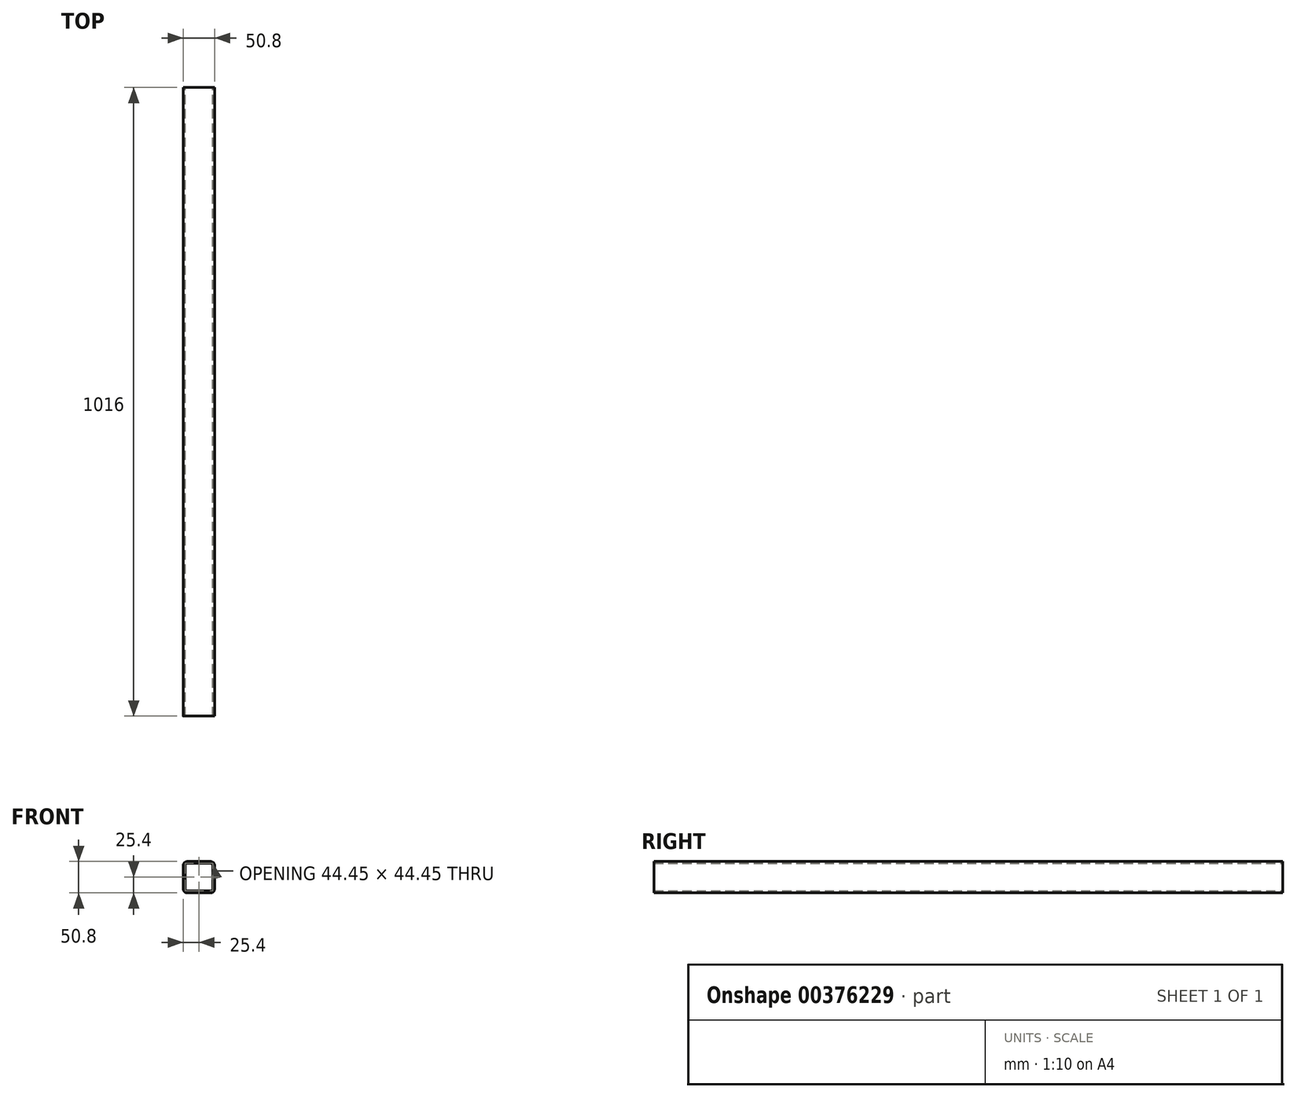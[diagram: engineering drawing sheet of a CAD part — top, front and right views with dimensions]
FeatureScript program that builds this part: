
annotation { "Feature Type Name" : "Feature", "Feature Type Description" : "" }
export const myFeature = defineFeature(function(context is Context, id is Id, definition is map)
    precondition{}
    {
        {
            var Q0;
            Q0=qCreatedBy(makeId("Front.planeOp"),FACE);
            var sketch = newSketch(context, id + "F0", { "sketchPlane" : qUnion([Q0])});
            skLineSegment(sketch, "E0.bottom", {"start": v(19.05, 25.4) * mm, "end": v(-19.05, 25.4) * mm});
            skLineSegment(sketch, "E0.top", {"start": v(19.05, -25.4) * mm, "end": v(-19.05, -25.4) * mm});
            skLineSegment(sketch, "E0.left", {"start": v(25.4, 19.05) * mm, "end": v(25.4, -19.05) * mm});
            skLineSegment(sketch, "E0.right", {"start": v(-25.4, 19.05) * mm, "end": v(-25.4, -19.05) * mm});
            skPoint(sketch, "E0.middle", {"position": v(0, 0) * mm});
            skPoint(sketch, "E1.visualSharp", {"position": v(-25.4, 25.4) * mm});
            skArc(sketch, "E1.filletArc", {"start": v(-19.05, 25.4) * mm, "mid": v(-23.54, 23.54) * mm, "end": v(-25.4, 19.05) * mm});
            skPoint(sketch, "E2.visualSharp", {"position": v(25.4, 25.4) * mm});
            skArc(sketch, "E2.filletArc", {"start": v(25.4, 19.05) * mm, "mid": v(23.54, 23.54) * mm, "end": v(19.05, 25.4) * mm});
            skPoint(sketch, "E3.visualSharp", {"position": v(25.4, -25.4) * mm});
            skArc(sketch, "E3.filletArc", {"start": v(19.05, -25.4) * mm, "mid": v(23.54, -23.54) * mm, "end": v(25.4, -19.05) * mm});
            skPoint(sketch, "E4.visualSharp", {"position": v(-25.4, -25.4) * mm});
            skArc(sketch, "E4.filletArc", {"start": v(-25.4, -19.05) * mm, "mid": v(-23.54, -23.54) * mm, "end": v(-19.05, -25.4) * mm});
            skArc(sketch, "E5.0", {"start": v(22.23, 19.05) * mm, "mid": v(21.3, 21.3) * mm, "end": v(19.05, 22.23) * mm});
            skLineSegment(sketch, "E5.1", {"start": v(22.23, 19.05) * mm, "end": v(22.23, -19.05) * mm});
            skLineSegment(sketch, "E5.2", {"start": v(19.05, 22.23) * mm, "end": v(-19.05, 22.23) * mm});
            skArc(sketch, "E5.3", {"start": v(19.05, -22.23) * mm, "mid": v(21.3, -21.3) * mm, "end": v(22.23, -19.05) * mm});
            skArc(sketch, "E5.4", {"start": v(-19.05, 22.23) * mm, "mid": v(-21.3, 21.3) * mm, "end": v(-22.22, 19.05) * mm});
            skLineSegment(sketch, "E5.5", {"start": v(-22.22, 19.05) * mm, "end": v(-22.22, -19.05) * mm});
            skArc(sketch, "E5.6", {"start": v(-22.22, -19.05) * mm, "mid": v(-21.3, -21.3) * mm, "end": v(-19.05, -22.23) * mm});
            skLineSegment(sketch, "E5.7", {"start": v(19.05, -22.23) * mm, "end": v(-19.05, -22.23) * mm});
            skSolve(sketch);
        }
        {
            var Q0;
            Q0 = qSketchRegion(id + "F0", true);
            extrude(context, id + "F1", {"entities" : qUnion([Q0]), "endBound" : BoundingType.SYMMETRIC, "depth" : 1016 * mm});
        }
    });
